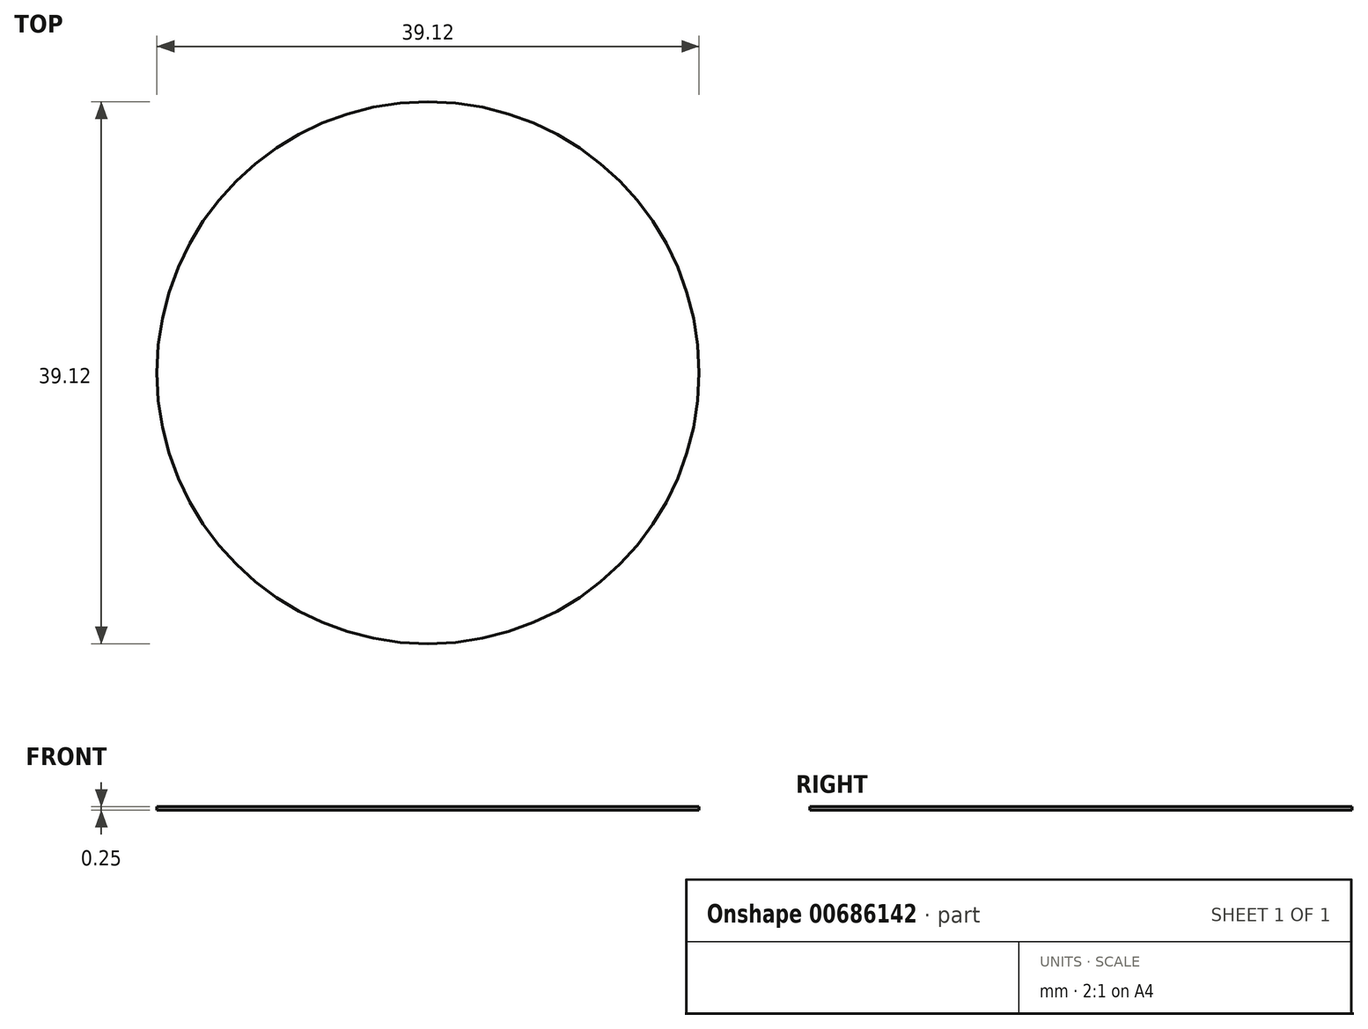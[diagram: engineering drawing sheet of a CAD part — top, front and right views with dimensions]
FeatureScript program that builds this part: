
annotation { "Feature Type Name" : "Feature", "Feature Type Description" : "" }
export const myFeature = defineFeature(function(context is Context, id is Id, definition is map)
    precondition{}
    {
        {
            var Q0;
            Q0=qCreatedBy(makeId("Top.planeOp"),FACE);
            var sketch = newSketch(context, id + "F0", { "sketchPlane" : qUnion([Q0])});
            skCircle(sketch, "E0", {"center": v(0, 0) * mm, "radius": 19.56 * mm});
            skSolve(sketch);
        }
        {
            var Q0;
            Q0=makeQuery(id+"F0.imprint","IMPRINT",FACE,{"disambiguationData":[TD([[makeQuery(id+"F0.imprint","IMPRINT",EDGE,{"derivedFrom":sQuery(id+"F0.wireOp",EDGE,"E0")}),1.0]])]});
            extrude(context, id + "F1", {"entities" : qUnion([Q0]), "depth" : 0.25 * mm, "offsetDistance" : 25.4 * mm});
        }
    });
